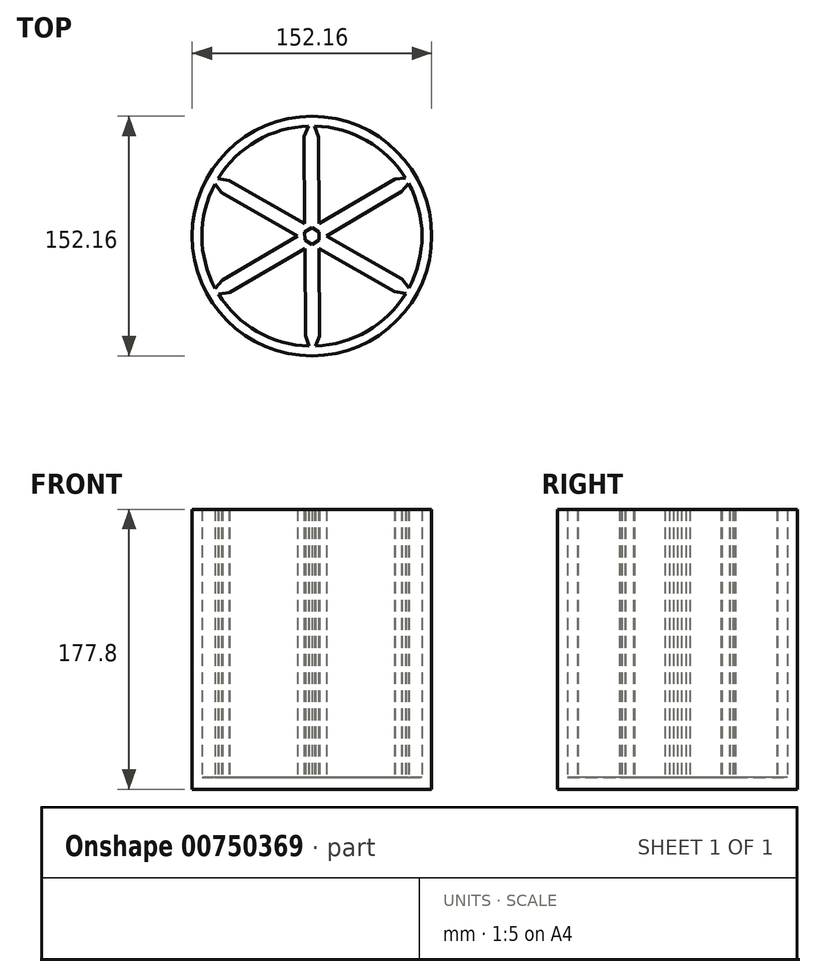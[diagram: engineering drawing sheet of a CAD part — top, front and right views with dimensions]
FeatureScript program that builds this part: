
annotation { "Feature Type Name" : "Feature", "Feature Type Description" : "" }
export const myFeature = defineFeature(function(context is Context, id is Id, definition is map)
    precondition{}
    {
        {
            var Q0;
            Q0=qCreatedBy(makeId("Top.planeOp"),FACE);
            var sketch = newSketch(context, id + "F0", { "sketchPlane" : qUnion([Q0])});
            skCircle(sketch, "E0", {"center": v(0, 0) * mm, "radius": 76.08 * mm});
            skSolve(sketch);
        }
        {
            var Q0;
            Q0=qCreatedBy(makeId("Top.planeOp"),FACE);
            var sketch = newSketch(context, id + "F1", { "sketchPlane" : qUnion([Q0])});
            skCircle(sketch, "E1", {"center": v(0, 0) * mm, "radius": 69.89 * mm});
            skSolve(sketch);
        }
        {
            var Q0;
            Q0=makeQuery(id+"F0.imprint","IMPRINT",FACE,{"disambiguationData":[TD([[makeQuery(id+"F0.imprint","IMPRINT",EDGE,{"derivedFrom":sQuery(id+"F0.wireOp",EDGE,"E0")}),1.0]])]});
            var sketch = newSketch(context, id + "F2", { "sketchPlane" : qUnion([Q0])});
            skPoint(sketch, "E2.center", {"position": v(0, 0) * mm});
            skLineSegment(sketch, "E3", {"start": v(0, 74.74) * mm, "end": v(-5, 63.32) * mm});
            skLineSegment(sketch, "E4", {"start": v(-5, 63.32) * mm, "end": v(0, 74.74) * mm});
            skLineSegment(sketch, "E5", {"start": v(0, 74.74) * mm, "end": v(4.25, 63.02) * mm});
            skLineSegment(sketch, "E6.2.0", {"start": v(4.87, -63.64) * mm, "end": v(0, -75.12) * mm});
            skLineSegment(sketch, "E6.2.1", {"start": v(0, -75.12) * mm, "end": v(-4.1, -63.34) * mm});
            skLineSegment(sketch, "E7", {"start": v(-5, 63.32) * mm, "end": v(-4.1, -63.34) * mm});
            skLineSegment(sketch, "E8", {"start": v(4.25, 63.02) * mm, "end": v(4.87, -63.64) * mm});
            skLineSegment(sketch, "E9.1.0", {"start": v(-52.34, -35.98) * mm, "end": v(-64.73, -37.37) * mm});
            skLineSegment(sketch, "E9.1.1", {"start": v(-64.73, -37.37) * mm, "end": v(-56.7, -27.83) * mm});
            skLineSegment(sketch, "E9.1.2", {"start": v(-52.34, -35.98) * mm, "end": v(56.9, 28.12) * mm});
            skLineSegment(sketch, "E9.1.3", {"start": v(-56.7, -27.83) * mm, "end": v(52.68, 36.04) * mm});
            skLineSegment(sketch, "E9.1.4", {"start": v(65.05, 37.56) * mm, "end": v(56.9, 28.12) * mm});
            skLineSegment(sketch, "E9.1.5", {"start": v(52.68, 36.04) * mm, "end": v(65.05, 37.56) * mm});
            skLineSegment(sketch, "E9.2.0", {"start": v(57.33, -27.33) * mm, "end": v(64.73, -37.37) * mm});
            skLineSegment(sketch, "E9.2.1", {"start": v(64.73, -37.37) * mm, "end": v(52.45, -35.2) * mm});
            skLineSegment(sketch, "E9.2.2", {"start": v(57.33, -27.33) * mm, "end": v(-52.8, 35.22) * mm});
            skLineSegment(sketch, "E9.2.3", {"start": v(52.45, -35.2) * mm, "end": v(-57.55, 27.6) * mm});
            skLineSegment(sketch, "E9.2.4", {"start": v(-65.05, 37.56) * mm, "end": v(-52.8, 35.22) * mm});
            skLineSegment(sketch, "E9.2.5", {"start": v(-57.55, 27.6) * mm, "end": v(-65.05, 37.56) * mm});
            skSolve(sketch);
        }
        {
            var Q0;
            Q0 = qSketchRegion(id + "F0", true);
            extrude(context, id + "F3", {"entities" : qUnion([Q0]), "depth" : 177.8 * mm, "offsetDistance" : 25.4 * mm});
        }
        {
            var Q0;
            Q0 = qSketchRegion(id + "F1", true);
            extrude(context, id + "F4", {"entities" : qUnion([Q0]), "operationType" : NewBodyOperationType.REMOVE, "depth" : 177.8 * mm, "offsetDistance" : 25.4 * mm, "hasSecondDirection" : true, "secondDirectionOppositeDirection" : true, "secondDirectionDepth" : 0 * mm});
        }
        {
            var Q0;
            Q0 = qSketchRegion(id + "F2", true);
            extrude(context, id + "F5", {"entities" : qUnion([Q0]), "operationType" : NewBodyOperationType.ADD, "depth" : 177.8 * mm, "offsetDistance" : 25.4 * mm, "hasSecondDirection" : true, "secondDirectionOppositeDirection" : false, "secondDirectionDepth" : 0 * mm});
        }
        {
            var Q0;
            Q0 = qSketchRegion(id + "F1", true);
            extrude(context, id + "F6", {"entities" : qUnion([Q0]), "operationType" : NewBodyOperationType.ADD, "depth" : 7.62 * mm, "offsetDistance" : 25.4 * mm});
        }
    });
